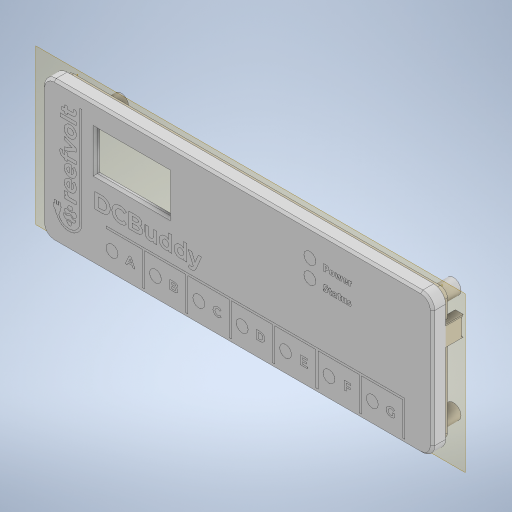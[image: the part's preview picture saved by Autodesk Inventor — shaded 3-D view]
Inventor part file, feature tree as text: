
AUTODESK INVENTOR PART (.ipt)
format: ipt  version: 2024.3 (Build 283343000, 343)  size: 1,717,760 bytes
history: native  units: in
note: dims shown in document units (in); Inventor stores cm internally (conversion verified against a paired STEP export)
features: reference x61, extrude x24, sketch x24, projected_geometry x20, other x18, plane x4, chamfer x3, fillet x2
ambient origin geometry x8: Origin, YZ Plane, XZ Plane, XY Plane, X Axis, Y Axis, Z Axis, Center Point
bodies: Body1 (feature_tree)
feature tree (156):
  plane  "Work Plane1"
  extrude  "Extrusion5"  Depth=0.0787in
  extrude  "Extrusion6"  Depth=0.0709in
  extrude  "Extrusion7"  Depth=0.0787in
  plane  "Work Plane4"
  plane  "Work Plane5"
  extrude  "Extrusion8"  Depth=0.1181in TaperAngle=0.0deg
  extrude  "Extrusion9"  Depth=0.1969in TaperAngle=0.0deg
  extrude  "Extrusion10"  Depth=0.1969in TaperAngle=0.0deg
  extrude  "Extrusion11"  Depth=0.315in TaperAngle=0.0deg
  extrude  "Extrusion12"  Depth=0.0394in TaperAngle=0.0deg
  extrude  "Extrusion13"  Depth=0.315in TaperAngle=0.0deg
  sketch  "Sketch15"  dims[d47=0.0394in d48=0.125in d49=45.0deg d50=0.0394in d51=0.125in d52=45.0deg]
  plane  "Work Plane6"
  extrude  "Extrusion14"  Depth=0.0394in TaperAngle=45.0deg
  extrude  "Extrusion15"  Depth=0.0039in
  chamfer  "Chamfer1"  Distance=0.0039in
  chamfer  "Chamfer2"  Distance=0.0039in
  fillet  "Fillet2"  Radius=0.0039in
  extrude  "Extrusion20"  Depth=0.0394in
  extrude  "Extrusion21"  Depth=0.0591in TaperAngle=0.0deg
  extrude  "Extrusion22"  Depth=0.3937in TaperAngle=0.0deg
  extrude  "Extrusion23"  Depth=0.0079in
  extrude  "Extrusion24"  Depth=0.3031in TaperAngle=0.0deg
  extrude  "Extrusion25"  Depth=0.0118in
  extrude  "Extrusion26"  Depth=0.0394in
  extrude  "Extrusion27"  Depth=0.0118in
  extrude  "Extrusion28"  Depth=0.0394in
  chamfer  "Chamfer3"  Distance=0.0004in
  fillet  "Fillet3"  Radius=0.2362in
  extrude  "Logo"  Depth=0.0787in
  extrude  "Extrusion30"  Depth=0.0004in TaperAngle=0.0deg
  extrude  "Extrusion31"  Depth=0.0004in TaperAngle=0.0deg
  extrude  "Extrusion32"  Depth=0.0394in
  sketch  "Sketch6"  dims[d15=0.1575in d16=0.0in d17=0.0787in]
  reference  "Reference30"
  reference  "Reference31"
  sketch  "Sketch7"  dims[d18=0.1969in d19=0.0in d20=0.0709in]
  sketch  "Sketch8"  dims[d21=0.1181in d22=0.0in d23=0.0787in]
  sketch  "Sketch9"  dims[d24=0.0787in d27=0.1181in d28=0.0in]
  sketch  "Sketch10"  dims[d29=0.3937in d30=0.0in d31=0.1969in d32=0.0in]
  sketch  "Sketch11"  dims[d33=0.1969in d34=0.1969in d35=0.0in]
  sketch  "Sketch12"  dims[d36=0.0787in d37=0.0in d38=0.315in d39=0.0in]
  sketch  "Sketch13"  dims[d40=0.2756in d41=0.0394in d42=0.0in]
  sketch  "Sketch14"  dims[d43=0.1575in d44=0.315in d45=0.0in]
  reference  "Reference62"
  reference  "Reference63"
  reference  "Reference64"
  reference  "Reference65"
  reference  "Reference66"
  sketch  "Sketch16"  dims[d62=0.0039in d63=0.0039in d64=0.0039in d65=0.0in d66=0.0039in d67=0.0in d68=0.0039in d69=0.0in]
  projected_geometry  "Projected Loop2"
  reference  "Reference67"
  reference  "Reference68"
  reference  "Reference71"
  reference  "Reference72"
  reference  "Reference73"
  reference  "Reference74"
  reference  "Reference75"
  reference  "Reference76"
  reference  "Reference77"
  reference  "Reference78"
  reference  "Reference79"
  reference  "Reference80"
  reference  "Reference81"
  reference  "Reference82"
  reference  "Reference83"
  reference  "Reference84"
  reference  "Reference85"
  reference  "Reference86"
  reference  "Reference87"
  reference  "Reference88"
  reference  "Reference89"
  reference  "Reference90"
  reference  "Reference91"
  reference  "Reference92"
  reference  "Reference93"
  reference  "Reference94"
  reference  "Reference95"
  reference  "Reference96"
  reference  "Reference97"
  reference  "Reference99"
  reference  "Reference100"
  reference  "Reference101"
  reference  "Reference102"
  reference  "Reference103"
  reference  "Reference104"
  reference  "Reference105"
  sketch  "Sketch21"  dims[d70=0.0039in d71=0.0in d72=0.0394in]
  projected_geometry  "Projected Loop7"
  sketch  "Sketch22"  dims[d73=0.2165in d74=0.0591in d75=0.0in]
  projected_geometry  "Projected Loop8"
  sketch  "Sketch23"  dims[d76=0.0394in d77=0.3937in d78=0.0in]
  projected_geometry  "Projected Loop9"
  sketch  "Sketch24"  dims[d79=0.0004in d80=0.0in d81=0.0079in]
  projected_geometry  "Projected Loop10"
  reference  "Reference106"
  sketch  "Sketch25"  dims[d82=0.0079in d83=0.3031in d84=0.0in]
  reference  "Reference107"
  reference  "Reference108"
  reference  "Reference109"
  reference  "Reference110"
  reference  "Reference111"
  reference  "Reference112"
  reference  "Reference113"
  reference  "Reference114"
  reference  "Reference115"
  sketch  "Sketch26"  dims[d85=0.0118in d86=0.0118in]
  projected_geometry  "Projected Loop11"
  projected_geometry  "Projected Loop12"
  projected_geometry  "Projected Loop13"
  projected_geometry  "Projected Loop14"
  projected_geometry  "Projected Loop15"
  projected_geometry  "Projected Loop16"
  sketch  "Sketch27"  dims[d87=0.3031in d88=0.0in d89=0.0394in]
  projected_geometry  "Projected Loop17"
  projected_geometry  "Projected Loop18"
  projected_geometry  "Projected Loop19"
  projected_geometry  "Projected Loop20"
  projected_geometry  "Projected Loop21"
  projected_geometry  "Projected Loop22"
  projected_geometry  "Projected Loop23"
  projected_geometry  "Projected Loop24"
  projected_geometry  "Projected Loop25"
  reference  "Reference116"
  reference  "Reference117"
  reference  "Reference118"
  reference  "Reference119"
  sketch  "Sketch28"  dims[d90=0.0118in d91=0.0787in d92=45.0deg d93=0.0118in]
  reference  "Reference120"
  reference  "Reference121"
  sketch  "Sketch29"  dims[d94=0.0004in d95=0.0in d97=0.0394in]
  reference  "Reference122"
  reference  "Reference123"
  sketch  "Sketch30"  dims[d98=0.5512in]
  sketch  "Sketch31"  dims[d99=0.0787in]
  sketch  "Sketch32"  dims[d100=2.7559in d102=0.7874in d103=0.3937in d105=0.3937in d107=0.0004in d108=0.0in d109=0.2362in]
  sketch  "Sketch33"  dims[d110=0.0787in d111=0.0787in d112=0.0004in d113=0.0in d114=0.0004in d115=0.0in d116=0.0394in d117=0.0202in d118=0.1919in]
  other  "<userpath>\Dropbox\elec\Mechanical\DCBuddyV2\PCB\_TOP_Design.iam"
  other  "_TOP_Design.iam"
  other  "DCB2_BottomShell:1"
  other  "dcbuddy_v2:1"
  other  "FP-43045-0802-MFG_CMP-002-00102-1:1"
  other  "OLED_With_Carrier:1"
  other  "User Library-OLED-1_3-128X64:1"
  other  "User Library-OLED-1_3-128X64_1"
  other  "LED5MM_CMP-130-0003-6:9"
  other  "LED5MM_CMP-130-0003-6:8"
  other  "LED5MM_CMP-130-0003-6:7"
  other  "LED5MM_CMP-130-0003-6:6"
  other  "LED5MM_CMP-130-0003-6:5"
  other  "LED5MM_CMP-130-0003-6:4"
  other  "LED5MM_CMP-130-0003-6:3"
  other  "LED5MM_CMP-130-0003-6:1"
  other  "LED5MM_CMP-130-0003-6:2"
  other  "AMPHENOL_10155435-00011LF_CMP-243-000000-3:1"
